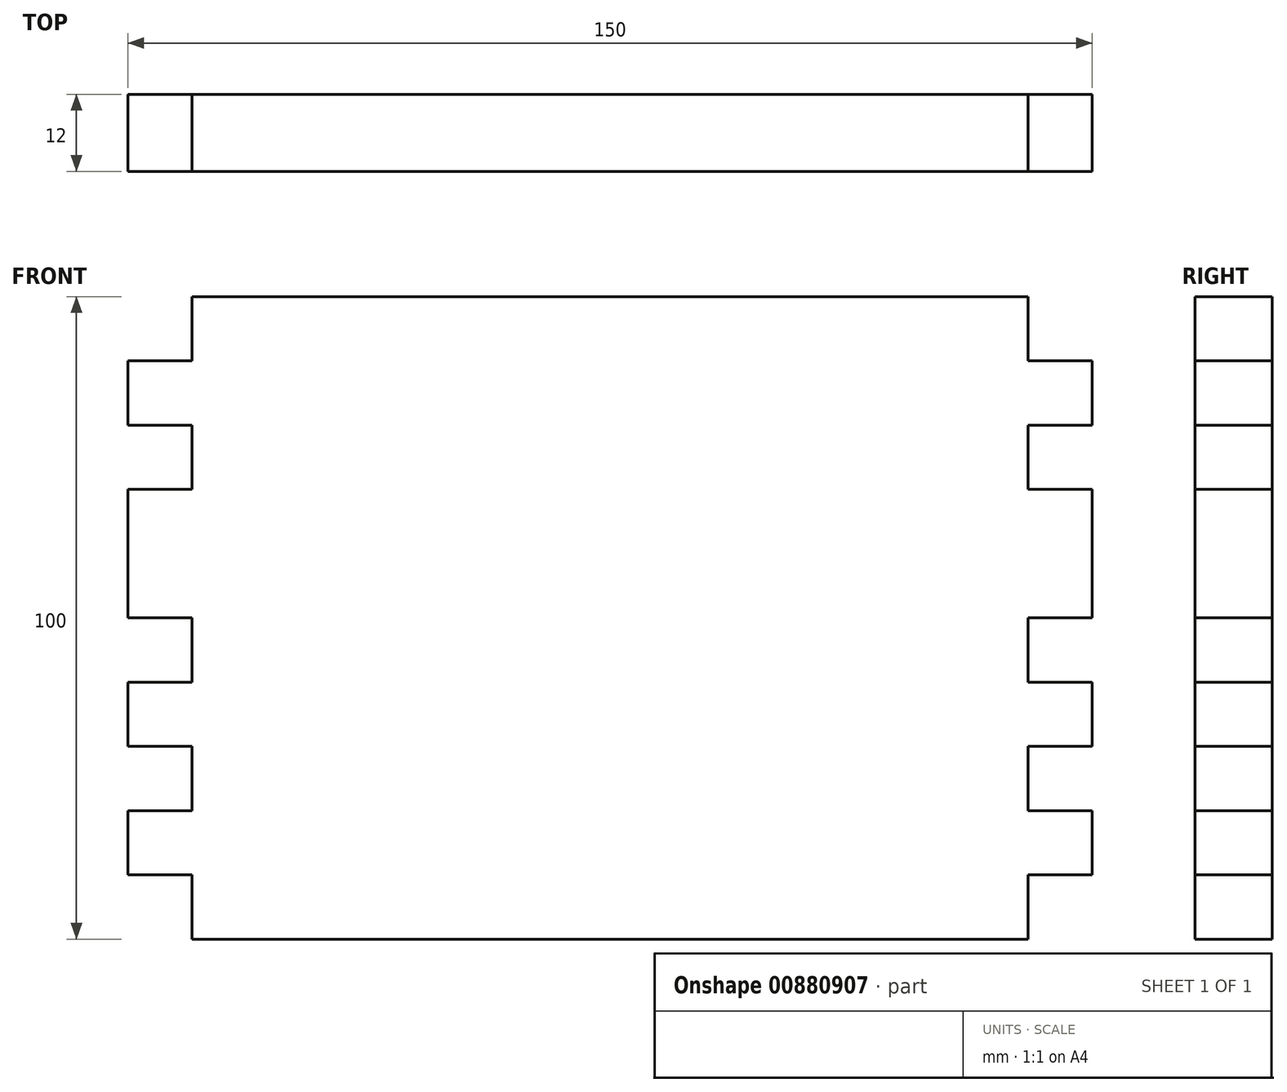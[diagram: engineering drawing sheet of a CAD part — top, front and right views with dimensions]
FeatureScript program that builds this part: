
annotation { "Feature Type Name" : "Feature", "Feature Type Description" : "" }
export const myFeature = defineFeature(function(context is Context, id is Id, definition is map)
    precondition{}
    {
        {
            var Q0;
            Q0=qCreatedBy(makeId("Front.planeOp"),FACE);
            var sketch = newSketch(context, id + "F0", { "sketchPlane" : qUnion([Q0])});
            skLineSegment(sketch, "E0.bottom", {"start": v(65, 50) * mm, "end": v(0, 50) * mm});
            skLineSegment(sketch, "E0.top", {"start": v(65, -50) * mm, "end": v(0, -50) * mm});
            skLineSegment(sketch, "E0.left", {"start": v(75, 40) * mm, "end": v(75, 30) * mm});
            skPoint(sketch, "E0.middle", {"position": v(0, 0) * mm});
            skLineSegment(sketch, "E1", {"start": v(65, 20) * mm, "end": v(65, 30) * mm});
            skLineSegment(sketch, "E2", {"start": v(65, 40) * mm, "end": v(75, 40) * mm});
            skLineSegment(sketch, "E3", {"start": v(65, 30) * mm, "end": v(75, 30) * mm});
            skLineSegment(sketch, "E4", {"start": v(75, 20) * mm, "end": v(65, 20) * mm});
            skPoint(sketch, "E5.orphan", {"position": v(75, 50) * mm});
            skLineSegment(sketch, "E6.trimOffspring", {"start": v(75, 10) * mm, "end": v(75, 0) * mm});
            skPoint(sketch, "E7.orphan", {"position": v(65, -50) * mm});
            skLineSegment(sketch, "E8", {"start": v(65, -50) * mm, "end": v(65, -40) * mm});
            skLineSegment(sketch, "E9", {"start": v(65, -40) * mm, "end": v(75, -40) * mm});
            skLineSegment(sketch, "E10", {"start": v(75, -40) * mm, "end": v(75, -30) * mm});
            skLineSegment(sketch, "E11", {"start": v(75, -30) * mm, "end": v(65, -30) * mm});
            skLineSegment(sketch, "E12", {"start": v(65, -30) * mm, "end": v(65, -20) * mm});
            skLineSegment(sketch, "E13", {"start": v(65, -20) * mm, "end": v(75, -20) * mm});
            skLineSegment(sketch, "E14", {"start": v(75, -20) * mm, "end": v(75, -10) * mm});
            skLineSegment(sketch, "E15", {"start": v(75, -10) * mm, "end": v(65, -10) * mm});
            skLineSegment(sketch, "E16", {"start": v(65, -10) * mm, "end": v(65, 0) * mm});
            skLineSegment(sketch, "E17", {"start": v(65, 0) * mm, "end": v(75, 0) * mm});
            skLineSegment(sketch, "E18", {"start": v(75, 0) * mm, "end": v(75, 10) * mm});
            skLineSegment(sketch, "E19", {"start": v(65, 20) * mm, "end": v(75, 20) * mm});
            skLineSegment(sketch, "E20", {"start": v(75, 30) * mm, "end": v(65, 30) * mm});
            skLineSegment(sketch, "E21", {"start": v(75, 30) * mm, "end": v(75, 40) * mm});
            skLineSegment(sketch, "E22.trimOffspring", {"start": v(75, -30) * mm, "end": v(75, -40) * mm});
            skLineSegment(sketch, "E23.trimOffspring", {"start": v(75, -10) * mm, "end": v(75, -20) * mm});
            skPoint(sketch, "E24.end.orphan", {"position": v(65, 10) * mm});
            skLineSegment(sketch, "E25", {"start": v(75, 10) * mm, "end": v(75, 20) * mm});
            skPoint(sketch, "E26.orphan", {"position": v(75, -50) * mm});
            skLineSegment(sketch, "E27", {"start": v(0, 50) * mm, "end": v(0, -50) * mm});
            skPoint(sketch, "E0.right.end.orphan", {"position": v(-75, -50) * mm});
            skPoint(sketch, "E0.right.start.orphan", {"position": v(-75, 50) * mm});
            skLineSegment(sketch, "E28.MirrorCS", {"start": v(-75, -10) * mm, "end": v(-75, -20) * mm});
            skLineSegment(sketch, "E29.MirrorCS", {"start": v(-65, 30) * mm, "end": v(-75, 30) * mm});
            skLineSegment(sketch, "E30.MirrorCS", {"start": v(-75, 20) * mm, "end": v(-65, 20) * mm});
            skLineSegment(sketch, "E31.MirrorCS", {"start": v(-75, 40) * mm, "end": v(-75, 30) * mm});
            skLineSegment(sketch, "E32.MirrorCS", {"start": v(-75, 10) * mm, "end": v(-75, 0) * mm});
            skLineSegment(sketch, "E33.MirrorCS", {"start": v(-65, 40) * mm, "end": v(-75, 40) * mm});
            skLineSegment(sketch, "E34.MirrorCS", {"start": v(-75, -30) * mm, "end": v(-75, -40) * mm});
            skLineSegment(sketch, "E35.MirrorCS", {"start": v(-65, 20) * mm, "end": v(-65, 30) * mm});
            skLineSegment(sketch, "E36.MirrorCS", {"start": v(-75, 10) * mm, "end": v(-75, 20) * mm});
            skLineSegment(sketch, "E37.MirrorCS", {"start": v(-65, 50) * mm, "end": v(0, 50) * mm});
            skPoint(sketch, "E38.MirrorP", {"position": v(-65, -50) * mm});
            skLineSegment(sketch, "E39.MirrorCS", {"start": v(-75, 30) * mm, "end": v(-75, 40) * mm});
            skLineSegment(sketch, "E40.MirrorCS", {"start": v(-75, -30) * mm, "end": v(-65, -30) * mm});
            skLineSegment(sketch, "E41.MirrorCS", {"start": v(-65, 20) * mm, "end": v(-75, 20) * mm});
            skLineSegment(sketch, "E42.MirrorCS", {"start": v(-65, -50) * mm, "end": v(0, -50) * mm});
            skPoint(sketch, "E43.MirrorP", {"position": v(-65, 10) * mm});
            skLineSegment(sketch, "E44.MirrorCS", {"start": v(-65, -30) * mm, "end": v(-65, -20) * mm});
            skLineSegment(sketch, "E45.MirrorCS", {"start": v(-75, 30) * mm, "end": v(-65, 30) * mm});
            skLineSegment(sketch, "E46.MirrorCS", {"start": v(-75, -40) * mm, "end": v(-75, -30) * mm});
            skLineSegment(sketch, "E47.MirrorCS", {"start": v(-65, 0) * mm, "end": v(-75, 0) * mm});
            skLineSegment(sketch, "E48.MirrorCS", {"start": v(-65, -40) * mm, "end": v(-75, -40) * mm});
            skLineSegment(sketch, "E49.MirrorCS", {"start": v(-75, -10) * mm, "end": v(-65, -10) * mm});
            skLineSegment(sketch, "E50.MirrorCS", {"start": v(-65, -10) * mm, "end": v(-65, 0) * mm});
            skLineSegment(sketch, "E51.MirrorCS", {"start": v(-75, 0) * mm, "end": v(-75, 10) * mm});
            skLineSegment(sketch, "E52.MirrorCS", {"start": v(-75, -20) * mm, "end": v(-75, -10) * mm});
            skLineSegment(sketch, "E53.MirrorCS", {"start": v(-65, -20) * mm, "end": v(-75, -20) * mm});
            skLineSegment(sketch, "E54.MirrorCS", {"start": v(-65, -50) * mm, "end": v(-65, -40) * mm});
            skLineSegment(sketch, "E55.trimOffspring", {"start": v(65, 40) * mm, "end": v(65, 50) * mm});
            skLineSegment(sketch, "E56.trimOffspring", {"start": v(-65, 40) * mm, "end": v(-65, 50) * mm});
            skSolve(sketch);
        }
        {
            var Q0;
            Q0=makeQuery(id+"F0.imprint","IMPRINT",FACE,{"disambiguationData":[TD([[makeQuery(id+"F0.imprint","IMPRINT",EDGE,{"derivedFrom":sQuery(id+"F0.wireOp",EDGE,"E27")}),-1.0]])]});
            var Q1;
            Q1=makeQuery(id+"F0.imprint","IMPRINT",FACE,{"disambiguationData":[TD([[makeQuery(id+"F0.imprint","IMPRINT",EDGE,{"derivedFrom":sQuery(id+"F0.wireOp",EDGE,"E0.bottom")}),1.0]])]});
            extrude(context, id + "F1", {"entities" : qUnion([Q0, Q1]), "depth" : 12 * mm, "offsetDistance" : 25 * mm});
        }
    });
